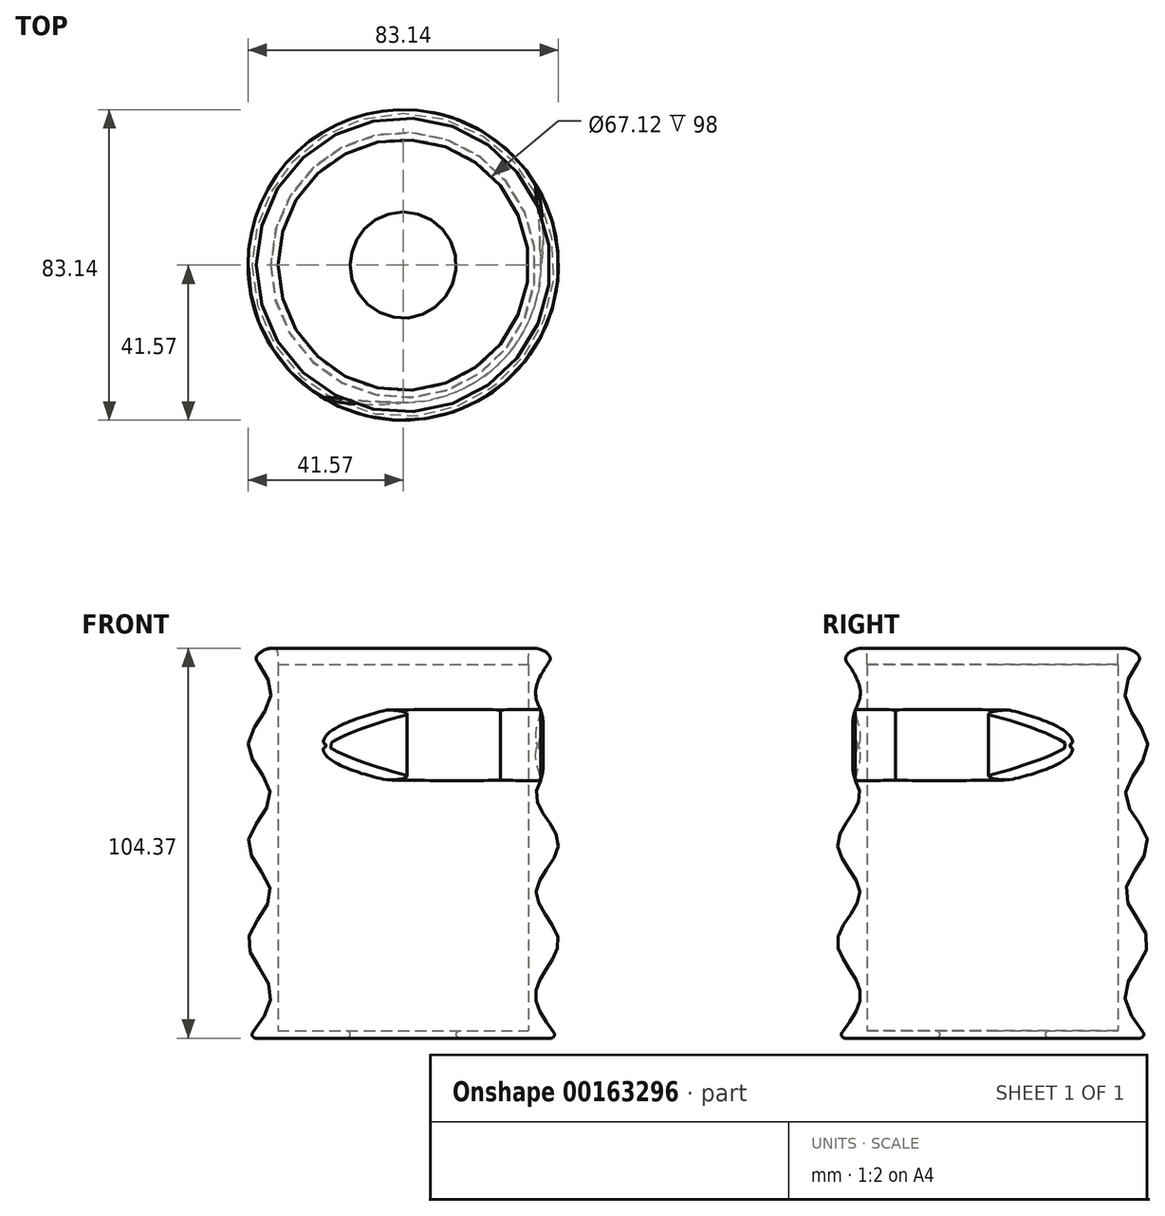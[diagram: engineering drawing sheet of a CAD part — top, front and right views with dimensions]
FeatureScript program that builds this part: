
annotation { "Feature Type Name" : "Feature", "Feature Type Description" : "" }
export const myFeature = defineFeature(function(context is Context, id is Id, definition is map)
    precondition{}
    {
        {
            var Q0;
            Q0=qCreatedBy(makeId("Front.planeOp"),FACE);
            var sketch = newSketch(context, id + "F0", { "sketchPlane" : qUnion([Q0])});
            skLineSegment(sketch, "E0", {"start": v(33.56, 0) * mm, "end": v(33.56, 100) * mm});
            skLineSegment(sketch, "E1", {"start": v(0, 13) * mm, "end": v(106.96, 13) * mm, "construction": true});
            skLineSegment(sketch, "E2.0.1.0", {"start": v(0, 26) * mm, "end": v(106.96, 26) * mm, "construction": true});
            skLineSegment(sketch, "E2.0.2.0", {"start": v(0, 39) * mm, "end": v(106.96, 39) * mm, "construction": true});
            skLineSegment(sketch, "E2.0.3.0", {"start": v(0, 52) * mm, "end": v(106.96, 52) * mm, "construction": true});
            skLineSegment(sketch, "E2.0.4.0", {"start": v(0, 65) * mm, "end": v(106.96, 65) * mm, "construction": true});
            skLineSegment(sketch, "E2.0.5.0", {"start": v(0, 78) * mm, "end": v(106.96, 78) * mm, "construction": true});
            skLineSegment(sketch, "E2.0.6.0", {"start": v(0, 91) * mm, "end": v(106.96, 91) * mm, "construction": true});
            skLineSegment(sketch, "E2.0.7.0", {"start": v(0, 104) * mm, "end": v(106.96, 104) * mm, "construction": true});
            skLineSegment(sketch, "E2.1.0.0", {"start": v(25, 13.02) * mm, "end": v(131.96, 13.02) * mm, "construction": true});
            skLineSegment(sketch, "E2.1.1.0", {"start": v(25, 26.02) * mm, "end": v(131.96, 26.02) * mm, "construction": true});
            skLineSegment(sketch, "E2.1.2.0", {"start": v(25, 39.02) * mm, "end": v(131.96, 39.02) * mm, "construction": true});
            skLineSegment(sketch, "E2.1.3.0", {"start": v(25, 52.02) * mm, "end": v(131.96, 52.02) * mm, "construction": true});
            skLineSegment(sketch, "E2.1.4.0", {"start": v(25, 65.02) * mm, "end": v(131.96, 65.02) * mm, "construction": true});
            skLineSegment(sketch, "E2.1.5.0", {"start": v(25, 78.02) * mm, "end": v(131.96, 78.02) * mm, "construction": true});
            skLineSegment(sketch, "E2.1.6.0", {"start": v(25, 91.02) * mm, "end": v(131.96, 91.02) * mm, "construction": true});
            skLineSegment(sketch, "E2.1.7.0", {"start": v(25, 104.02) * mm, "end": v(131.96, 104.02) * mm, "construction": true});
            skLineSegment(sketch, "E2.2.0.0", {"start": v(50, 13.04) * mm, "end": v(156.96, 13.04) * mm, "construction": true});
            skLineSegment(sketch, "E2.2.1.0", {"start": v(50, 26.04) * mm, "end": v(156.96, 26.04) * mm, "construction": true});
            skLineSegment(sketch, "E2.2.2.0", {"start": v(50, 39.04) * mm, "end": v(156.96, 39.04) * mm, "construction": true});
            skLineSegment(sketch, "E2.2.3.0", {"start": v(50, 52.04) * mm, "end": v(156.96, 52.04) * mm, "construction": true});
            skLineSegment(sketch, "E2.2.4.0", {"start": v(50, 65.04) * mm, "end": v(156.96, 65.04) * mm, "construction": true});
            skLineSegment(sketch, "E2.2.5.0", {"start": v(50, 78.04) * mm, "end": v(156.96, 78.04) * mm, "construction": true});
            skLineSegment(sketch, "E2.2.6.0", {"start": v(50, 91.04) * mm, "end": v(156.96, 91.04) * mm, "construction": true});
            skLineSegment(sketch, "E2.2.7.0", {"start": v(50, 104.04) * mm, "end": v(156.96, 104.04) * mm, "construction": true});
            skLineSegment(sketch, "E2.direction1", {"start": v(0, 13) * mm, "end": v(25, 13.02) * mm, "construction": true});
            skLineSegment(sketch, "E2.direction2", {"start": v(0, 13) * mm, "end": v(0, 26) * mm, "construction": true});
            skLineSegment(sketch, "E3", {"start": v(35.56, 0) * mm, "end": v(35.56, 104) * mm, "construction": true});
            skLineSegment(sketch, "E4", {"start": v(41.56, 0) * mm, "end": v(41.56, 104) * mm, "construction": true});
            skFitSpline(sketch, "E5", {"points": [v(41.56, 0) * mm, v(35.56, 13.02) * mm, v(41.56, 26.02) * mm, v(35.56, 39.02) * mm, v(41.56, 52) * mm, v(35.56, 65.02) * mm, v(41.56, 78.02) * mm, v(35.56, 91.02) * mm, v(41.56, 104) * mm], "startDerivative": vector(-83.13, 104) * mm, "endDerivative": vector(79.7, 106.64) * mm});
            skLineSegment(sketch, "E6", {"start": v(39.49, 0) * mm, "end": v(15.2, 0) * mm});
            skLineSegment(sketch, "E7", {"start": v(33.56, 2) * mm, "end": v(15.2, 2) * mm});
            skArc(sketch, "E8", {"start": v(15.2, 2) * mm, "mid": v(14.2, 1) * mm, "end": v(15.2, 0) * mm});
            skArc(sketch, "E9.filletArc", {"start": v(39.49, 0) * mm, "mid": v(40.39, 0.56) * mm, "end": v(40.28, 1.62) * mm});
            skFitSpline(sketch, "E10", {"points": [v(38.24, 99.56) * mm, v(39.33, 101.88) * mm, v(36.82, 104.02) * mm, v(34.09, 104.02) * mm, v(33.56, 100) * mm], "startDerivative": vector(8.23, 10.2) * mm, "endDerivative": vector(-0.32, -18.98) * mm});
            skLineSegment(sketch, "E11", {"start": v(0, 0) * mm, "end": v(0, 131.89) * mm, "construction": true});
            skSolve(sketch);
        }
        {
            var Q0;
            Q0 = qSketchRegion(id + "F0", true);
            var Q1;
            Q1=sQuery(id+"F0.wireOp",EDGE,"E11");
            revolve(context, id + "F1", {"entities" : qUnion([Q0]), "axis" : qUnion([Q1]), "revolveType" : RevolveType.FULL});
        }
        {
            var Q0;
            Q0=qCreatedBy(makeId("Top.planeOp"),FACE);
            cPlane(context, id + "F2", {"entities" : qUnion([Q0]), "cplaneType" : CPlaneType.OFFSET, "offset" : 78.04 * mm, "width" : 150 * mm, "height" : 150 * mm});
        }
        {
            var Q0;
            Q0=qCreatedBy(id+"F2.planeOp",FACE);
            var sketch = newSketch(context, id + "F3", { "sketchPlane" : qUnion([Q0])});
            skCircle(sketch, "E12.0", {"center": v(0, 0) * mm, "radius": 33.56 * mm, "construction": true});
            skLineSegment(sketch, "E13.0", {"start": v(33.7, -11.35) * mm, "end": v(33.7, -11.35) * mm});
            skArc(sketch, "E14.0", {"start": v(-11.24, -40.01) * mm, "mid": v(32.82, -25.5) * mm, "end": v(36, 20.78) * mm, "construction": true});
            skLineSegment(sketch, "E15", {"start": v(32.98, 57.43) * mm, "end": v(-39.05, -67.33) * mm, "construction": true});
            skLineSegment(sketch, "E16", {"start": v(0, 0) * mm, "end": v(47.47, 27.4) * mm, "construction": true});
            skLineSegment(sketch, "E17", {"start": v(0, 0) * mm, "end": v(44.35, -44.35) * mm, "construction": true});
            skLineSegment(sketch, "E18.trimOffspring", {"start": v(25.12, -25.12) * mm, "end": v(25.12, -25.12) * mm});
            skPoint(sketch, "E19.10.internal.orphan", {"position": v(38.56, 0) * mm});
            skArc(sketch, "E20", {"start": v(-20.78, -36) * mm, "mid": v(30.75, -30.75) * mm, "end": v(36, 20.78) * mm});
            skCircle(sketch, "E21", {"center": v(0, 0) * mm, "radius": 39.35 * mm, "construction": true});
            skCircle(sketch, "E22.0", {"center": v(0, 0) * mm, "radius": 36.85 * mm, "construction": true});
            skPoint(sketch, "E23.orphan", {"position": v(25.12, -25.12) * mm});
            skPoint(sketch, "E24.MirrorCS.3.internal.orphan", {"position": v(37.05, -6.67) * mm});
            skArc(sketch, "E25", {"start": v(-20.78, -36) * mm, "mid": v(-20.85, -35.95) * mm, "end": v(-20.91, -35.92) * mm});
            skArc(sketch, "E26", {"start": v(-20.78, -36) * mm, "mid": v(-9.9, -37.4) * mm, "end": v(1.06, -36.83) * mm});
            skArc(sketch, "E27", {"start": v(1.06, -36.83) * mm, "mid": v(14.57, -33.8) * mm, "end": v(26.06, -26.06) * mm});
            skArc(sketch, "E28.MirrorCS", {"start": v(36, 20.78) * mm, "mid": v(37.4, 9.9) * mm, "end": v(36.83, -1.06) * mm});
            skArc(sketch, "E29.MirrorCS", {"start": v(36.83, -1.06) * mm, "mid": v(33.8, -14.57) * mm, "end": v(26.06, -26.06) * mm});
            skSolve(sketch);
        }
        {
            var Q0;
            Q0 = qSketchRegion(id + "F3", true);
            extrude(context, id + "F4", {"entities" : qUnion([Q0]), "operationType" : NewBodyOperationType.REMOVE, "endBound" : BoundingType.SYMMETRIC, "oppositeDirection" : true, "depth" : 25 * mm});
        }
        {
            var Q0;
            Q0=makeQuery(id+"F4.boolean.opBoolean","INTERSECT",EDGE,{"disambiguationData":[OD(1.0)],"derivedFrom":[makeQuery(id+"F1.opRevolve","SWEPT_FACE",FACE,{"disambiguationData":[OSD([sQuery(id+"F0.wireOp",EDGE,"E5")])]}),makeQuery(id+"F4.opExtrude","SWEPT_FACE",FACE,{"disambiguationData":[OSD([sQuery(id+"F3.wireOp",EDGE,"E28.MirrorCS")])]})]});
            fillet(context, id + "F5", {"entities" : qUnion([Q0]), "radius" : 5 * mm, "tangentPropagation" : true, "allowEdgeOverflow" : false});
        }
        {
            var Q0;
            Q0=makeQuery(id+"F4.boolean.opBoolean","INTERSECT",EDGE,{"disambiguationData":[OD(0.0)],"derivedFrom":[makeQuery(id+"F1.opRevolve","SWEPT_FACE",FACE,{"disambiguationData":[OSD([sQuery(id+"F0.wireOp",EDGE,"E5")])]}),makeQuery(id+"F4.opExtrude","SWEPT_FACE",FACE,{"disambiguationData":[OSD([sQuery(id+"F3.wireOp",EDGE,"E26")])]})]});
            fillet(context, id + "F6", {"entities" : qUnion([Q0]), "radius" : 5 * mm, "tangentPropagation" : true, "allowEdgeOverflow" : false});
        }
    });
